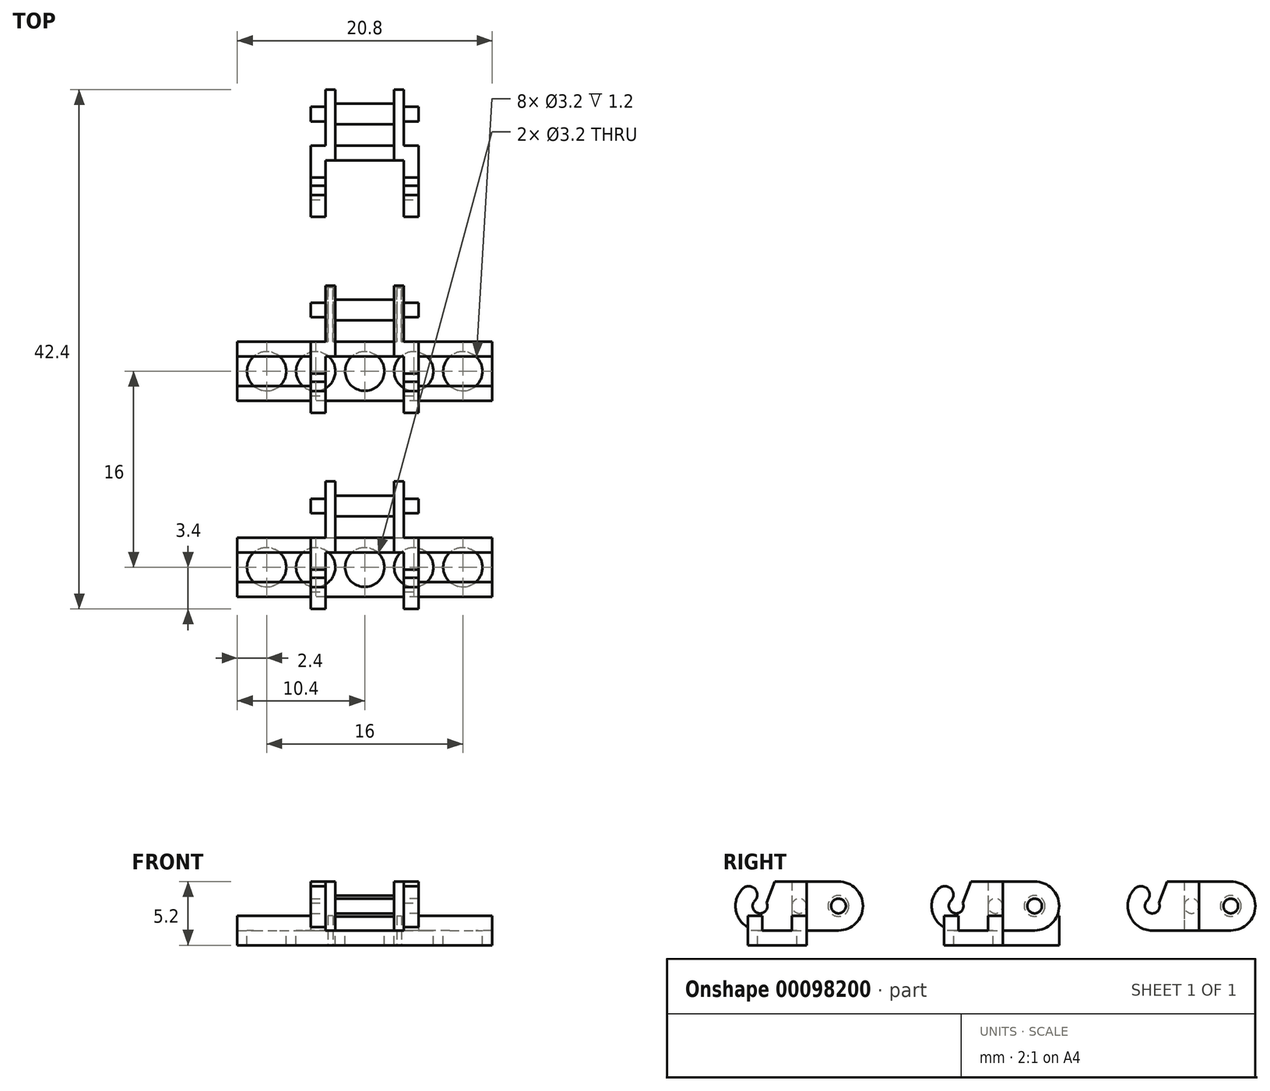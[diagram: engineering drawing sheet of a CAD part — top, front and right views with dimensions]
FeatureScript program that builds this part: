
annotation { "Feature Type Name" : "Feature", "Feature Type Description" : "" }
export const myFeature = defineFeature(function(context is Context, id is Id, definition is map)
    precondition{}
    {
        {
            var Q0;
            Q0=qCreatedBy(makeId("Top.planeOp"),FACE);
            var sketch = newSketch(context, id + "F0", { "sketchPlane" : qUnion([Q0])});
            skLineSegment(sketch, "E0.bottom", {"start": v(-4.4, 0) * mm, "end": v(-3.2, 0) * mm});
            skLineSegment(sketch, "E0.top", {"start": v(-4.4, -5.8) * mm, "end": v(-3.2, -5.8) * mm});
            skLineSegment(sketch, "E0.left", {"start": v(-4.4, 0) * mm, "end": v(-4.4, -5.8) * mm});
            skLineSegment(sketch, "E0.right", {"start": v(-3.2, -1.2) * mm, "end": v(-3.2, -5.8) * mm});
            skLineSegment(sketch, "E1.bottom", {"start": v(-3.2, -1.2) * mm, "end": v(-2.4, -1.2) * mm});
            skLineSegment(sketch, "E1.top", {"start": v(-3.2, 4.6) * mm, "end": v(-2.4, 4.6) * mm});
            skLineSegment(sketch, "E1.left", {"start": v(-3.2, 0) * mm, "end": v(-3.2, 4.6) * mm});
            skLineSegment(sketch, "E1.right", {"start": v(-2.4, -1.2) * mm, "end": v(-2.4, 4.6) * mm});
            skLineSegment(sketch, "E2.MirrorCS", {"start": v(4.4, -5.8) * mm, "end": v(3.2, -5.8) * mm});
            skLineSegment(sketch, "E3.MirrorCS", {"start": v(2.4, -1.2) * mm, "end": v(2.4, 4.6) * mm});
            skLineSegment(sketch, "E4.MirrorCS", {"start": v(4.4, 0) * mm, "end": v(3.2, 0) * mm});
            skLineSegment(sketch, "E5.MirrorCS", {"start": v(3.2, 0) * mm, "end": v(3.2, 4.6) * mm});
            skLineSegment(sketch, "E6.MirrorCS", {"start": v(3.2, 4.6) * mm, "end": v(2.4, 4.6) * mm});
            skLineSegment(sketch, "E7.MirrorCS", {"start": v(3.2, -1.2) * mm, "end": v(2.4, -1.2) * mm});
            skLineSegment(sketch, "E8.MirrorCS", {"start": v(4.4, 0) * mm, "end": v(4.4, -5.8) * mm});
            skLineSegment(sketch, "E9.MirrorCS", {"start": v(3.2, -1.2) * mm, "end": v(3.2, -5.8) * mm});
            skSolve(sketch);
        }
        {
            var Q0;
            Q0 = qSketchRegion(id + "F0", true);
            extrude(context, id + "F1", {"entities" : qUnion([Q0]), "depth" : 4 * mm});
        }
        {
            var Q0;
            Q0=makeQuery(id+"F1.opExtrude","CAP_EDGE",EDGE,{"disambiguationData":[OSD([sQuery(id+"F0.wireOp",EDGE,"E0.top")])],"isStart":false});
            var Q1;
            Q1=makeQuery(id+"F1.opExtrude","CAP_EDGE",EDGE,{"disambiguationData":[OSD([sQuery(id+"F0.wireOp",EDGE,"E0.top")])],"isStart":true});
            var Q2;
            Q2=makeQuery(id+"F1.opExtrude","CAP_EDGE",EDGE,{"disambiguationData":[OSD([sQuery(id+"F0.wireOp",EDGE,"E2.MirrorCS")])],"isStart":false});
            var Q3;
            Q3=makeQuery(id+"F1.opExtrude","CAP_EDGE",EDGE,{"disambiguationData":[OSD([sQuery(id+"F0.wireOp",EDGE,"E2.MirrorCS")])],"isStart":true});
            var Q4;
            Q4=makeQuery(id+"F1.opExtrude","CAP_EDGE",EDGE,{"disambiguationData":[OSD([sQuery(id+"F0.wireOp",EDGE,"E6.MirrorCS")])],"isStart":false});
            var Q5;
            Q5=makeQuery(id+"F1.opExtrude","CAP_EDGE",EDGE,{"disambiguationData":[OSD([sQuery(id+"F0.wireOp",EDGE,"E6.MirrorCS")])],"isStart":true});
            var Q6;
            Q6=makeQuery(id+"F1.opExtrude","CAP_EDGE",EDGE,{"disambiguationData":[OSD([sQuery(id+"F0.wireOp",EDGE,"E1.top")])],"isStart":true});
            var Q7;
            Q7=makeQuery(id+"F1.opExtrude","CAP_EDGE",EDGE,{"disambiguationData":[OSD([sQuery(id+"F0.wireOp",EDGE,"E1.top")])],"isStart":false});
            fillet(context, id + "F2", {"entities" : qUnion([Q0, Q1, Q2, Q3, Q4, Q5, Q6, Q7]), "radius" : 2 * mm, "tangentPropagation" : true, "allowEdgeOverflow" : false});
        }
        {
            var Q0;
            Q0=makeQuery(id+"F1.opExtrude","SWEPT_FACE",FACE,{"disambiguationData":[OSD([sQuery(id+"F0.wireOp",EDGE,"E5.MirrorCS")])]});
            var sketch = newSketch(context, id + "F3", { "sketchPlane" : qUnion([Q0])});
            skCircle(sketch, "E10", {"center": v(2.6, 2) * mm, "radius": 0.6 * mm});
            skSolve(sketch);
        }
        {
            var Q0;
            Q0=makeQuery(id+"F1.opExtrude","SWEPT_FACE",FACE,{"disambiguationData":[OSD([sQuery(id+"F0.wireOp",EDGE,"E1.left")])]});
            var sketch = newSketch(context, id + "F4", { "sketchPlane" : qUnion([Q0])});
            skCircle(sketch, "E11", {"center": v(-2.6, 2) * mm, "radius": 0.6 * mm});
            skSolve(sketch);
        }
        {
            var Q0;
            Q0=makeQuery(id+"F3.imprint","IMPRINT",FACE,{"disambiguationData":[TD([[makeQuery(id+"F3.imprint","IMPRINT",EDGE,{"derivedFrom":sQuery(id+"F3.wireOp",EDGE,"E10")}),1.0]])]});
            extrude(context, id + "F5", {"entities" : qUnion([Q0]), "operationType" : NewBodyOperationType.ADD, "depth" : 1.2 * mm});
        }
        {
            var Q0;
            Q0=makeQuery(id+"F4.imprint","IMPRINT",FACE,{"disambiguationData":[TD([[makeQuery(id+"F4.imprint","IMPRINT",EDGE,{"derivedFrom":sQuery(id+"F4.wireOp",EDGE,"E11")}),1.0]])]});
            extrude(context, id + "F6", {"entities" : qUnion([Q0]), "operationType" : NewBodyOperationType.ADD, "depth" : 1.2 * mm});
        }
        {
            var Q0;
            Q0=makeQuery(id+"F1.opExtrude","SWEPT_FACE",FACE,{"disambiguationData":[OSD([sQuery(id+"F0.wireOp",EDGE,"E1.right")])]});
            var sketch = newSketch(context, id + "F7", { "sketchPlane" : qUnion([Q0])});
            skCircle(sketch, "E12", {"center": v(2.6, 2) * mm, "radius": 0.85 * mm});
            skCircle(sketch, "E13", {"center": v(-0.6, 2) * mm, "radius": 0.6 * mm});
            skSolve(sketch);
        }
        {
            var Q0;
            Q0=makeQuery(id+"F7.imprint","IMPRINT",FACE,{"disambiguationData":[TD([[makeQuery(id+"F7.imprint","IMPRINT",EDGE,{"derivedFrom":sQuery(id+"F7.wireOp",EDGE,"E12")}),1.0]])]});
            var Q1;
            Q1=makeQuery(id+"F7.imprint","IMPRINT",FACE,{"disambiguationData":[TD([[makeQuery(id+"F7.imprint","IMPRINT",EDGE,{"derivedFrom":sQuery(id+"F7.wireOp",EDGE,"E13")}),1.0]])]});
            extrude(context, id + "F8", {"entities" : qUnion([Q0, Q1]), "operationType" : NewBodyOperationType.ADD, "depth" : 4.8 * mm});
        }
        {
            var Q0;
            Q0=makeQuery(id+"F1.opExtrude","SWEPT_FACE",FACE,{"disambiguationData":[OSD([sQuery(id+"F0.wireOp",EDGE,"E8.MirrorCS")])]});
            var sketch = newSketch(context, id + "F9", { "sketchPlane" : qUnion([Q0])});
            skArc(sketch, "E14", {"start": v(-4.22, 2.42) * mm, "mid": v(-3.91, 1.41) * mm, "end": v(-3.25, 2.24) * mm});
            skArc(sketch, "E15", {"start": v(-4.22, 2.42) * mm, "mid": v(-4.23, 3.41) * mm, "end": v(-5.22, 3.41) * mm});
            skPoint(sketch, "E15.first.point", {"position": v(-4.22, 2.42) * mm});
            skPoint(sketch, "E15.second.point", {"position": v(-4.02, 2.92) * mm});
            skPoint(sketch, "E15.third.point", {"position": v(-5.22, 3.41) * mm});
            skLineSegment(sketch, "E16", {"start": v(-2.6, 4) * mm, "end": v(-3.25, 2.24) * mm});
            skSolve(sketch);
        }
        {
            var Q0;
            Q0=makeQuery(id+"F9.imprint","IMPRINT",FACE,{"disambiguationData":[TD([[makeQuery(id+"F9.imprint","IMPRINT",EDGE,{"derivedFrom":sQuery(id+"F9.wireOp",EDGE,"E14")}),1.0]])]});
            extrude(context, id + "F10", {"entities" : qUnion([Q0]), "operationType" : NewBodyOperationType.REMOVE, "oppositeDirection" : true, "depth" : 25 * mm});
        }
        {
            var Q0;
            Q0=makeQuery(id+"F1.opExtrude","SWEPT_BODY",BODY,{"disambiguationData":[OSD([sQuery(id+"F0.wireOp",EDGE,"E0.bottom"),sQuery(id+"F0.wireOp",EDGE,"E0.top"),sQuery(id+"F0.wireOp",EDGE,"E0.left"),sQuery(id+"F0.wireOp",EDGE,"E0.right"),sQuery(id+"F0.wireOp",EDGE,"E1.bottom"),sQuery(id+"F0.wireOp",EDGE,"E1.top"),sQuery(id+"F0.wireOp",EDGE,"E1.left"),sQuery(id+"F0.wireOp",EDGE,"E1.right")])]});
            transform(context, id + "F11", {"entities" : qUnion([Q0]), "transformType" : TransformType.TRANSLATION_3D, "dx" : 0 * mm, "dy" : 16 * mm, "dz" : 0 * mm, "makeCopy" : true});
        }
        {
            var Q0;
            Q0=qCreatedBy(makeId("Top.planeOp"),FACE);
            var sketch = newSketch(context, id + "F12", { "sketchPlane" : qUnion([Q0])});
            skLineSegment(sketch, "E17.bottom", {"start": v(-10.4, 0) * mm, "end": v(10.4, 0) * mm});
            skLineSegment(sketch, "E17.top", {"start": v(-10.4, -4.8) * mm, "end": v(10.4, -4.8) * mm});
            skLineSegment(sketch, "E17.left", {"start": v(-10.4, 0) * mm, "end": v(-10.4, -4.8) * mm});
            skLineSegment(sketch, "E17.right", {"start": v(10.4, 0) * mm, "end": v(10.4, -4.8) * mm});
            skCircle(sketch, "E18", {"center": v(0, -2.4) * mm, "radius": 1.6 * mm});
            skCircle(sketch, "E19", {"center": v(4, -2.4) * mm, "radius": 1.6 * mm});
            skCircle(sketch, "E20", {"center": v(8, -2.4) * mm, "radius": 1.6 * mm});
            skCircle(sketch, "E21", {"center": v(-4, -2.4) * mm, "radius": 1.6 * mm});
            skCircle(sketch, "E22", {"center": v(-8, -2.4) * mm, "radius": 1.6 * mm});
            skSolve(sketch);
        }
        {
            var Q0;
            Q0 = qSketchRegion(id + "F12", true);
            extrude(context, id + "F13", {"entities" : qUnion([Q0]), "operationType" : NewBodyOperationType.ADD, "oppositeDirection" : true, "depth" : 1.2 * mm});
        }
        {
            var Q0;
            Q0=makeQuery(id+"F13.opExtrude","CAP_FACE",FACE,{"disambiguationData":[OSD([sQuery(id+"F12.wireOp",EDGE,"E17.bottom"),sQuery(id+"F12.wireOp",EDGE,"E17.top"),sQuery(id+"F12.wireOp",EDGE,"E17.left"),sQuery(id+"F12.wireOp",EDGE,"E17.right"),sQuery(id+"F12.wireOp",EDGE,"E18"),sQuery(id+"F12.wireOp",EDGE,"E19"),sQuery(id+"F12.wireOp",EDGE,"E20"),sQuery(id+"F12.wireOp",EDGE,"E21"),sQuery(id+"F12.wireOp",EDGE,"E22")])],"isStart":true});
            var sketch = newSketch(context, id + "F14", { "sketchPlane" : qUnion([Q0])});
            skLineSegment(sketch, "E23.bottom", {"start": v(-10.4, 0) * mm, "end": v(10.4, 0) * mm});
            skLineSegment(sketch, "E23.top", {"start": v(-10.4, -1.2) * mm, "end": v(10.4, -1.2) * mm});
            skLineSegment(sketch, "E23.left", {"start": v(-10.4, 0) * mm, "end": v(-10.4, -1.2) * mm});
            skLineSegment(sketch, "E23.right", {"start": v(10.4, 0) * mm, "end": v(10.4, -1.2) * mm});
            skLineSegment(sketch, "E24.bottom", {"start": v(-10.4, -4.8) * mm, "end": v(-3.2, -4.8) * mm});
            skLineSegment(sketch, "E24.top", {"start": v(-10.4, -3.6) * mm, "end": v(-3.2, -3.6) * mm});
            skLineSegment(sketch, "E24.left", {"start": v(-10.4, -4.8) * mm, "end": v(-10.4, -3.6) * mm});
            skLineSegment(sketch, "E24.right", {"start": v(-3.2, -4.8) * mm, "end": v(-3.2, -3.6) * mm});
            skLineSegment(sketch, "E25.bottom", {"start": v(10.4, -4.8) * mm, "end": v(3.2, -4.8) * mm});
            skLineSegment(sketch, "E25.top", {"start": v(10.4, -3.6) * mm, "end": v(3.2, -3.6) * mm});
            skLineSegment(sketch, "E25.left", {"start": v(10.4, -4.8) * mm, "end": v(10.4, -3.6) * mm});
            skLineSegment(sketch, "E25.right", {"start": v(3.2, -4.8) * mm, "end": v(3.2, -3.6) * mm});
            skLineSegment(sketch, "E26.bottom", {"start": v(-2.4, 0) * mm, "end": v(2.4, 0) * mm});
            skLineSegment(sketch, "E26.top", {"start": v(-2.4, -1.2) * mm, "end": v(2.4, -1.2) * mm});
            skLineSegment(sketch, "E26.left", {"start": v(-2.4, 0) * mm, "end": v(-2.4, -1.2) * mm});
            skLineSegment(sketch, "E26.right", {"start": v(2.4, 0) * mm, "end": v(2.4, -1.2) * mm});
            skSolve(sketch);
        }
        {
            var Q0;
            {var subQ0=sQuery(id+"F14.wireOp",EDGE,"E23.top");var subQ1=makeQuery(id+"F13.opExtrude","CAP_EDGE",EDGE,{"disambiguationData":[OSD([sQuery(id+"F12.wireOp",EDGE,"E22")])],"isStart":true});var subQ2=makeQuery(id+"F14.imprint","INTERSECT",VERTEX,{"disambiguationData":[OD(0.0)],"derivedFrom":[subQ1,subQ0]});Q0=makeQuery(id+"F14.imprint","IMPRINT",FACE,{"disambiguationData":[TD([[makeQuery(id+"F14.imprint","IMPRINT",EDGE,{"disambiguationData":[TD([[subQ2,-1.0]])],"derivedFrom":subQ0}),1.0]])]});}
            var Q1;
            {var subQ0=sQuery(id+"F14.wireOp",EDGE,"E23.top");var subQ1=makeQuery(id+"F13.opExtrude","CAP_EDGE",EDGE,{"disambiguationData":[OSD([sQuery(id+"F12.wireOp",EDGE,"E20")])],"isStart":true});var subQ2=makeQuery(id+"F14.imprint","INTERSECT",VERTEX,{"disambiguationData":[OD(0.0)],"derivedFrom":[subQ1,subQ0]});Q1=makeQuery(id+"F14.imprint","IMPRINT",FACE,{"disambiguationData":[TD([[makeQuery(id+"F14.imprint","IMPRINT",EDGE,{"disambiguationData":[TD([[subQ2,-1.0]])],"derivedFrom":subQ0}),1.0]])]});}
            var Q2;
            {var subQ0=sQuery(id+"F14.wireOp",EDGE,"E24.top");var subQ1=makeQuery(id+"F13.opExtrude","CAP_EDGE",EDGE,{"disambiguationData":[OSD([sQuery(id+"F12.wireOp",EDGE,"E22")])],"isStart":true});var subQ2=makeQuery(id+"F14.imprint","INTERSECT",VERTEX,{"disambiguationData":[OD(0.0)],"derivedFrom":[subQ1,subQ0]});Q2=makeQuery(id+"F14.imprint","IMPRINT",FACE,{"disambiguationData":[TD([[makeQuery(id+"F14.imprint","IMPRINT",EDGE,{"disambiguationData":[TD([[subQ2,-1.0]])],"derivedFrom":subQ0}),-1.0]])]});}
            var Q3;
            {var subQ0=sQuery(id+"F14.wireOp",EDGE,"E25.top");var subQ1=makeQuery(id+"F13.opExtrude","CAP_EDGE",EDGE,{"disambiguationData":[OSD([sQuery(id+"F12.wireOp",EDGE,"E20")])],"isStart":true});var subQ2=makeQuery(id+"F14.imprint","INTERSECT",VERTEX,{"disambiguationData":[OD(0.0)],"derivedFrom":[subQ1,subQ0]});Q3=makeQuery(id+"F14.imprint","IMPRINT",FACE,{"disambiguationData":[TD([[makeQuery(id+"F14.imprint","IMPRINT",EDGE,{"disambiguationData":[TD([[subQ2,-1.0]])],"derivedFrom":subQ0}),1.0]])]});}
            var Q4;
            {var subQ11=sQuery(id+"F14.wireOp",EDGE,"E24.right");var subQ14=sQuery(id+"F14.wireOp",EDGE,"E24.top");var subQ15=makeQuery(id+"F14.imprint","INTERSECT",VERTEX,{"derivedFrom":[subQ14,subQ11]});Q4=makeQuery(id+"F14.imprint","IMPRINT",FACE,{"disambiguationData":[TD([[makeQuery(id+"F14.imprint","IMPRINT",EDGE,{"disambiguationData":[TD([[subQ15,1.0]])],"derivedFrom":subQ14}),-1.0]])]});}
            var Q5;
            {var subQ11=sQuery(id+"F14.wireOp",EDGE,"E25.right");var subQ15=sQuery(id+"F14.wireOp",EDGE,"E25.top");var subQ17=makeQuery(id+"F14.imprint","INTERSECT",VERTEX,{"derivedFrom":[subQ15,subQ11]});Q5=makeQuery(id+"F14.imprint","IMPRINT",FACE,{"disambiguationData":[TD([[makeQuery(id+"F14.imprint","IMPRINT",EDGE,{"disambiguationData":[TD([[subQ17,1.0]])],"derivedFrom":subQ15}),1.0]])]});}
            var Q6;
            {var subQ0=sQuery(id+"F14.wireOp",EDGE,"E26.left");Q6=makeQuery(id+"F14.imprint","IMPRINT",FACE,{"disambiguationData":[TD([[makeQuery(id+"F14.imprint","IMPRINT",EDGE,{"derivedFrom":subQ0}),1.0]])]});}
            var Q7;
            {var subQ0=sQuery(id+"F14.wireOp",EDGE,"E26.right");Q7=makeQuery(id+"F14.imprint","IMPRINT",FACE,{"disambiguationData":[TD([[makeQuery(id+"F14.imprint","IMPRINT",EDGE,{"derivedFrom":subQ0}),-1.0]])]});}
            var Q8;
            {var subQ0=sQuery(id+"F14.wireOp",EDGE,"E23.left");Q8=makeQuery(id+"F14.imprint","IMPRINT",FACE,{"disambiguationData":[TD([[makeQuery(id+"F14.imprint","IMPRINT",EDGE,{"derivedFrom":subQ0}),1.0]])]});}
            var Q9;
            {var subQ0=sQuery(id+"F14.wireOp",EDGE,"E23.right");Q9=makeQuery(id+"F14.imprint","IMPRINT",FACE,{"disambiguationData":[TD([[makeQuery(id+"F14.imprint","IMPRINT",EDGE,{"derivedFrom":subQ0}),-1.0]])]});}
            var Q10;
            {var subQ19=sQuery(id+"F14.wireOp",EDGE,"E24.bottom");Q10=makeQuery(id+"F14.imprint","IMPRINT",FACE,{"disambiguationData":[TD([[makeQuery(id+"F14.imprint","IMPRINT",EDGE,{"derivedFrom":subQ19}),1.0]])]});}
            var Q11;
            {var subQ19=sQuery(id+"F14.wireOp",EDGE,"E25.bottom");Q11=makeQuery(id+"F14.imprint","IMPRINT",FACE,{"disambiguationData":[TD([[makeQuery(id+"F14.imprint","IMPRINT",EDGE,{"derivedFrom":subQ19}),1.0]])]});}
            extrude(context, id + "F15", {"entities" : qUnion([Q0, Q1, Q2, Q3, Q4, Q5, Q6, Q7, Q8, Q9, Q10, Q11]), "operationType" : NewBodyOperationType.ADD, "depth" : 1.2 * mm});
        }
        {
            var Q0;
            Q0=makeQuery(id+"F1.opExtrude","SWEPT_BODY",BODY,{"disambiguationData":[OSD([sQuery(id+"F0.wireOp",EDGE,"E0.bottom"),sQuery(id+"F0.wireOp",EDGE,"E0.top"),sQuery(id+"F0.wireOp",EDGE,"E0.left"),sQuery(id+"F0.wireOp",EDGE,"E0.right"),sQuery(id+"F0.wireOp",EDGE,"E1.bottom"),sQuery(id+"F0.wireOp",EDGE,"E1.top"),sQuery(id+"F0.wireOp",EDGE,"E1.left"),sQuery(id+"F0.wireOp",EDGE,"E1.right")])]});
            transform(context, id + "F16", {"entities" : qUnion([Q0]), "transformType" : TransformType.TRANSLATION_3D, "dx" : 0 * mm, "dy" : -16 * mm, "dz" : 0 * mm, "makeCopy" : true});
        }
        {
            var Q0;
            {var subQ0=sQuery(id+"F0.wireOp",EDGE,"E1.right");var subQ1=sQuery(id+"F0.wireOp",EDGE,"E1.left");var subQ3=sQuery(id+"F0.wireOp",EDGE,"E0.bottom");var subQ4=sQuery(id+"F0.wireOp",EDGE,"E1.top");Q0=makeQuery(id+"F13.boolean.opBoolean","SPLIT",FACE,{"disambiguationData":[TD([makeQuery(id+"F1.opExtrude","SWEPT_FACE",FACE,{"disambiguationData":[OSD([subQ3])]})])],"derivedFrom":makeQuery(id+"F1.opExtrude","CAP_FACE",FACE,{"disambiguationData":[OSD([subQ3,sQuery(id+"F0.wireOp",EDGE,"E0.top"),sQuery(id+"F0.wireOp",EDGE,"E0.left"),sQuery(id+"F0.wireOp",EDGE,"E0.right"),sQuery(id+"F0.wireOp",EDGE,"E1.bottom"),subQ4,subQ1,subQ0])],"isStart":true})});}
            var sketch = newSketch(context, id + "F17", { "sketchPlane" : qUnion([Q0])});
            skLineSegment(sketch, "E27.bottom", {"start": v(-3, 0) * mm, "end": v(-2.6, 0) * mm});
            skLineSegment(sketch, "E27.top", {"start": v(-3, -4.6) * mm, "end": v(-2.6, -4.6) * mm});
            skLineSegment(sketch, "E27.left", {"start": v(-3, 0) * mm, "end": v(-3, -4.6) * mm});
            skLineSegment(sketch, "E27.right", {"start": v(-2.6, 0) * mm, "end": v(-2.6, -4.6) * mm});
            skLineSegment(sketch, "E28.MirrorCS", {"start": v(2.6, 0) * mm, "end": v(2.6, -4.6) * mm});
            skLineSegment(sketch, "E29.MirrorCS", {"start": v(3, 0) * mm, "end": v(3, -4.6) * mm});
            skLineSegment(sketch, "E30.MirrorCS", {"start": v(3, -4.6) * mm, "end": v(2.6, -4.6) * mm});
            skLineSegment(sketch, "E31.MirrorCS", {"start": v(3, 0) * mm, "end": v(2.6, 0) * mm});
            skSolve(sketch);
        }
        {
            var Q0;
            {var subQ0=sQuery(id+"F17.wireOp",EDGE,"E27.bottom");Q0=makeQuery(id+"F17.imprint","IMPRINT",FACE,{"disambiguationData":[TD([[makeQuery(id+"F17.imprint","IMPRINT",EDGE,{"derivedFrom":subQ0}),-1.0]])]});}
            var Q1;
            {var subQ0=sQuery(id+"F17.wireOp",EDGE,"E27.top");Q1=makeQuery(id+"F17.imprint","IMPRINT",FACE,{"disambiguationData":[TD([[makeQuery(id+"F17.imprint","IMPRINT",EDGE,{"derivedFrom":subQ0}),1.0]])]});}
            var Q2;
            Q2=makeQuery(id+"F17.imprint","IMPRINT",FACE,{"disambiguationData":[TD([[makeQuery(id+"F17.imprint","IMPRINT",EDGE,{"derivedFrom":sQuery(id+"F17.wireOp",EDGE,"E28.MirrorCS")}),1.0]])]});
            extrude(context, id + "F18", {"entities" : qUnion([Q0, Q1, Q2]), "operationType" : NewBodyOperationType.ADD, "endBound" : BoundingType.SYMMETRIC, "oppositeDirection" : true, "depth" : 2.4 * mm});
        }
    });
